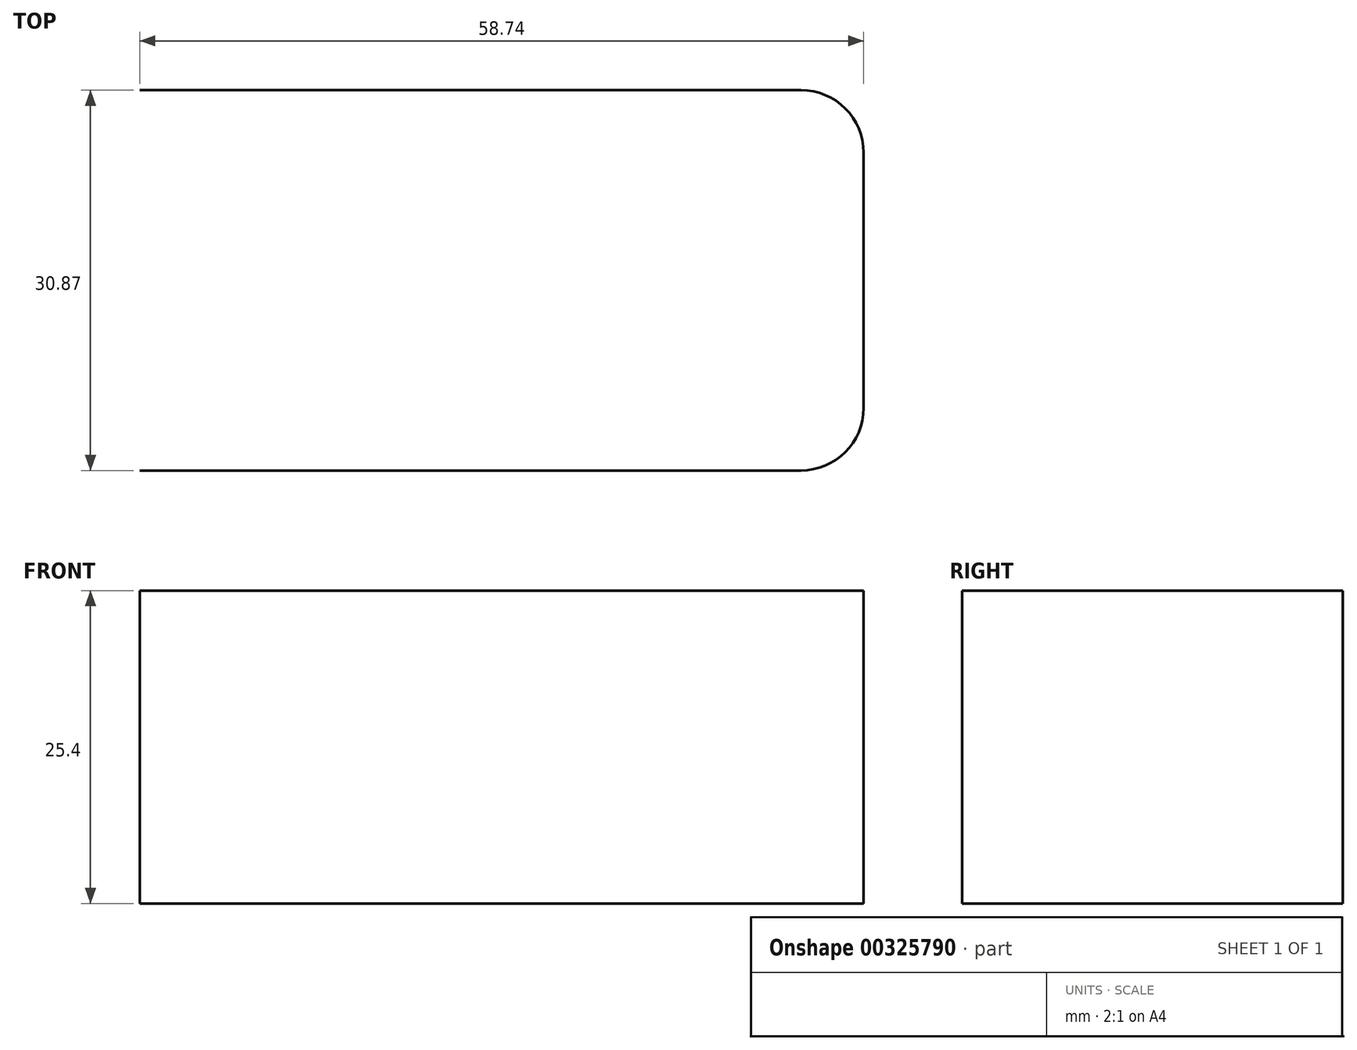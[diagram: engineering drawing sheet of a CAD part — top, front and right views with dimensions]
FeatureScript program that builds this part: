
annotation { "Feature Type Name" : "Feature", "Feature Type Description" : "" }
export const myFeature = defineFeature(function(context is Context, id is Id, definition is map)
    precondition{}
    {
        {
            var Q0;
            Q0=qCreatedBy(makeId("Top.planeOp"),FACE);
            var sketch = newSketch(context, id + "F0", { "sketchPlane" : qUnion([Q0])});
            skLineSegment(sketch, "E0.bottom", {"start": v(0, 15.32) * mm, "end": v(-58.74, 15.32) * mm});
            skLineSegment(sketch, "E0.top", {"start": v(0, 46.2) * mm, "end": v(-58.74, 46.2) * mm});
            skLineSegment(sketch, "E0.left", {"start": v(0, 15.32) * mm, "end": v(0, 46.2) * mm});
            skLineSegment(sketch, "E0.right", {"start": v(-58.74, 15.32) * mm, "end": v(-58.74, 46.2) * mm});
            skSolve(sketch);
        }
        {
            var Q0;
            Q0=sQuery(id+"F0.wireOp",EDGE,"E0.bottom");
            var Q1;
            Q1=sQuery(id+"F0.wireOp",EDGE,"E0.left");
            var Q2;
            Q2=sQuery(id+"F0.wireOp",EDGE,"E0.top");
            extrude(context, id + "F1", {"bodyType" : ToolBodyType.SURFACE, "surfaceEntities" : qUnion([Q0, Q1, Q2]), "depth" : 25.4 * mm});
        }
        {
            var Q0;
            Q0=makeQuery(id+"F1.opExtrude","SWEPT_EDGE",EDGE,{"disambiguationData":[OSD([sQuery(id+"F0.wireOp",VERTEX,"E0.left.start")])]});
            var Q1;
            Q1=makeQuery(id+"F1.opExtrude","SWEPT_EDGE",EDGE,{"disambiguationData":[OSD([sQuery(id+"F0.wireOp",VERTEX,"E0.top.start")])]});
            fillet(context, id + "F2", {"entities" : qUnion([Q0, Q1]), "radius" : 5.08 * mm, "tangentPropagation" : true, "allowEdgeOverflow" : false});
        }
    });
